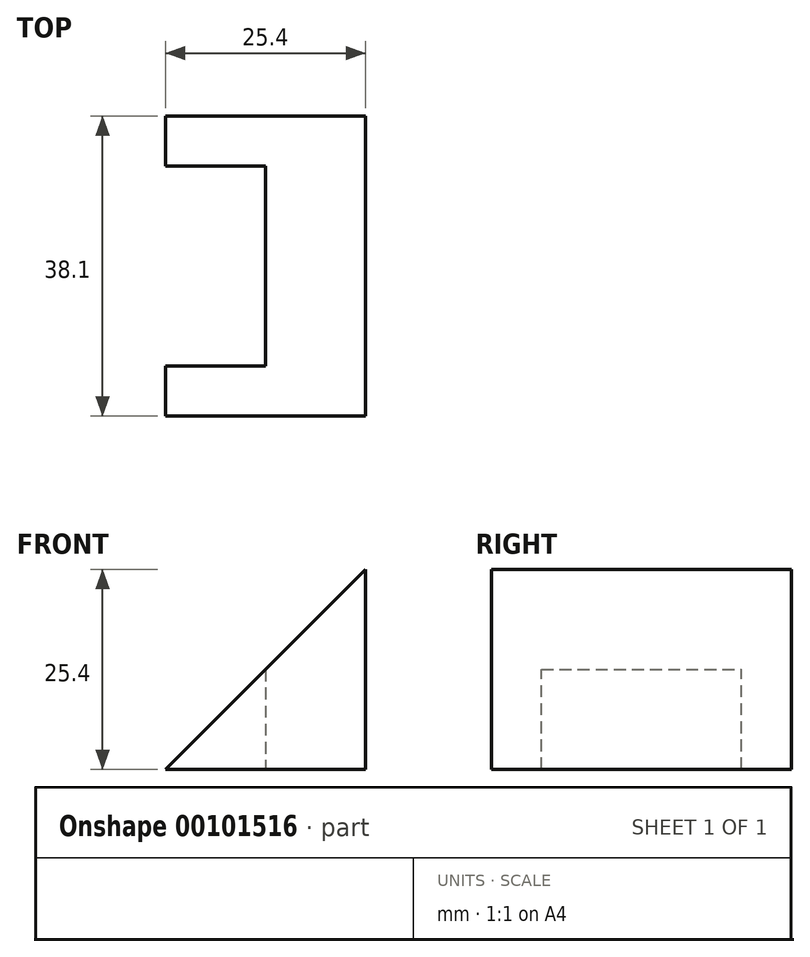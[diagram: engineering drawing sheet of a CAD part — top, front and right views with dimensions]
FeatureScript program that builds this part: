
annotation { "Feature Type Name" : "Feature", "Feature Type Description" : "" }
export const myFeature = defineFeature(function(context is Context, id is Id, definition is map)
    precondition{}
    {
        {
            var Q0;
            Q0=qCreatedBy(makeId("Front.planeOp"),FACE);
            var sketch = newSketch(context, id + "F0", { "sketchPlane" : qUnion([Q0])});
            skLineSegment(sketch, "E0", {"start": v(0, 0) * mm, "end": v(-25.4, 0) * mm});
            skLineSegment(sketch, "E1", {"start": v(-25.4, 0) * mm, "end": v(0, 25.4) * mm});
            skLineSegment(sketch, "E2", {"start": v(0, 25.4) * mm, "end": v(0, 0) * mm});
            skSolve(sketch);
        }
        {
            var Q0;
            Q0=makeQuery(id+"F0.imprint","IMPRINT",FACE,{"disambiguationData":[TD([[makeQuery(id+"F0.imprint","IMPRINT",EDGE,{"derivedFrom":sQuery(id+"F0.wireOp",EDGE,"E0")}),-1.0]])]});
            extrude(context, id + "F1", {"entities" : qUnion([Q0]), "depth" : 38.1 * mm});
        }
        {
            var Q0;
            Q0=qCreatedBy(makeId("Top.planeOp"),FACE);
            var sketch = newSketch(context, id + "F2", { "sketchPlane" : qUnion([Q0])});
            skLineSegment(sketch, "E3.bottom", {"start": v(0, 0) * mm, "end": v(-12.7, 0) * mm});
            skLineSegment(sketch, "E3.top", {"start": v(0, -6.35) * mm, "end": v(-12.7, -6.35) * mm});
            skLineSegment(sketch, "E3.left", {"start": v(0, 0) * mm, "end": v(0, -6.35) * mm});
            skLineSegment(sketch, "E3.right", {"start": v(-12.7, 0) * mm, "end": v(-12.7, -6.35) * mm});
            skLineSegment(sketch, "E4.bottom", {"start": v(-12.7, -6.35) * mm, "end": v(-25.4, -6.35) * mm});
            skLineSegment(sketch, "E4.top", {"start": v(-12.7, -31.75) * mm, "end": v(-25.4, -31.75) * mm});
            skLineSegment(sketch, "E4.left", {"start": v(-12.7, -6.35) * mm, "end": v(-12.7, -31.75) * mm});
            skLineSegment(sketch, "E4.right", {"start": v(-25.4, -6.35) * mm, "end": v(-25.4, -31.75) * mm});
            skSolve(sketch);
        }
        {
            var Q0;
            Q0=makeQuery(id+"F2.imprint","IMPRINT",FACE,{"disambiguationData":[TD([[makeQuery(id+"F2.imprint","IMPRINT",EDGE,{"derivedFrom":sQuery(id+"F2.wireOp",EDGE,"E4.bottom")}),1.0]])]});
            extrude(context, id + "F3", {"entities" : qUnion([Q0]), "operationType" : NewBodyOperationType.REMOVE, "endBound" : BoundingType.THROUGH_ALL, "depth" : 25.4 * mm});
        }
    });
